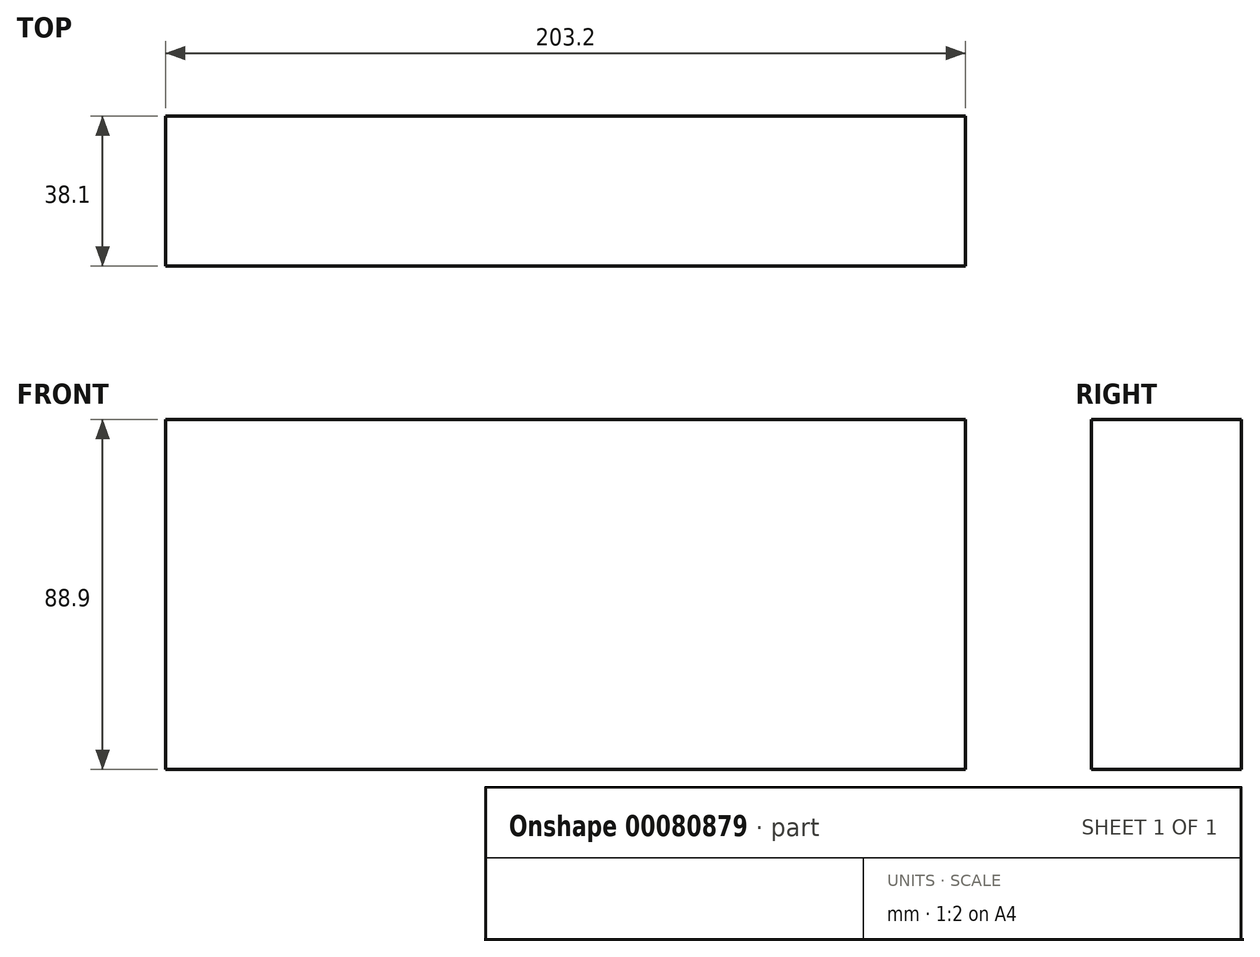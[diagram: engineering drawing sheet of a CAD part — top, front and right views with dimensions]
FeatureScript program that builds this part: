
annotation { "Feature Type Name" : "Feature", "Feature Type Description" : "" }
export const myFeature = defineFeature(function(context is Context, id is Id, definition is map)
    precondition{}
    {
        {
            var Q0;
            Q0=qCreatedBy(makeId("Front.planeOp"),FACE);
            var sketch = newSketch(context, id + "F0", { "sketchPlane" : qUnion([Q0])});
            skLineSegment(sketch, "E0", {"start": v(0, 0) * mm, "end": v(203.2, 0) * mm});
            skLineSegment(sketch, "E1", {"start": v(203.2, 0) * mm, "end": v(203.2, 88.9) * mm});
            skLineSegment(sketch, "E2", {"start": v(203.2, 88.9) * mm, "end": v(0, 88.9) * mm});
            skLineSegment(sketch, "E3", {"start": v(0, 88.9) * mm, "end": v(0, 0) * mm});
            skSolve(sketch);
        }
        {
            var Q0;
            Q0 = qSketchRegion(id + "F0", true);
            extrude(context, id + "F1", {"entities" : qUnion([Q0]), "depth" : 38.1 * mm});
        }
    });
